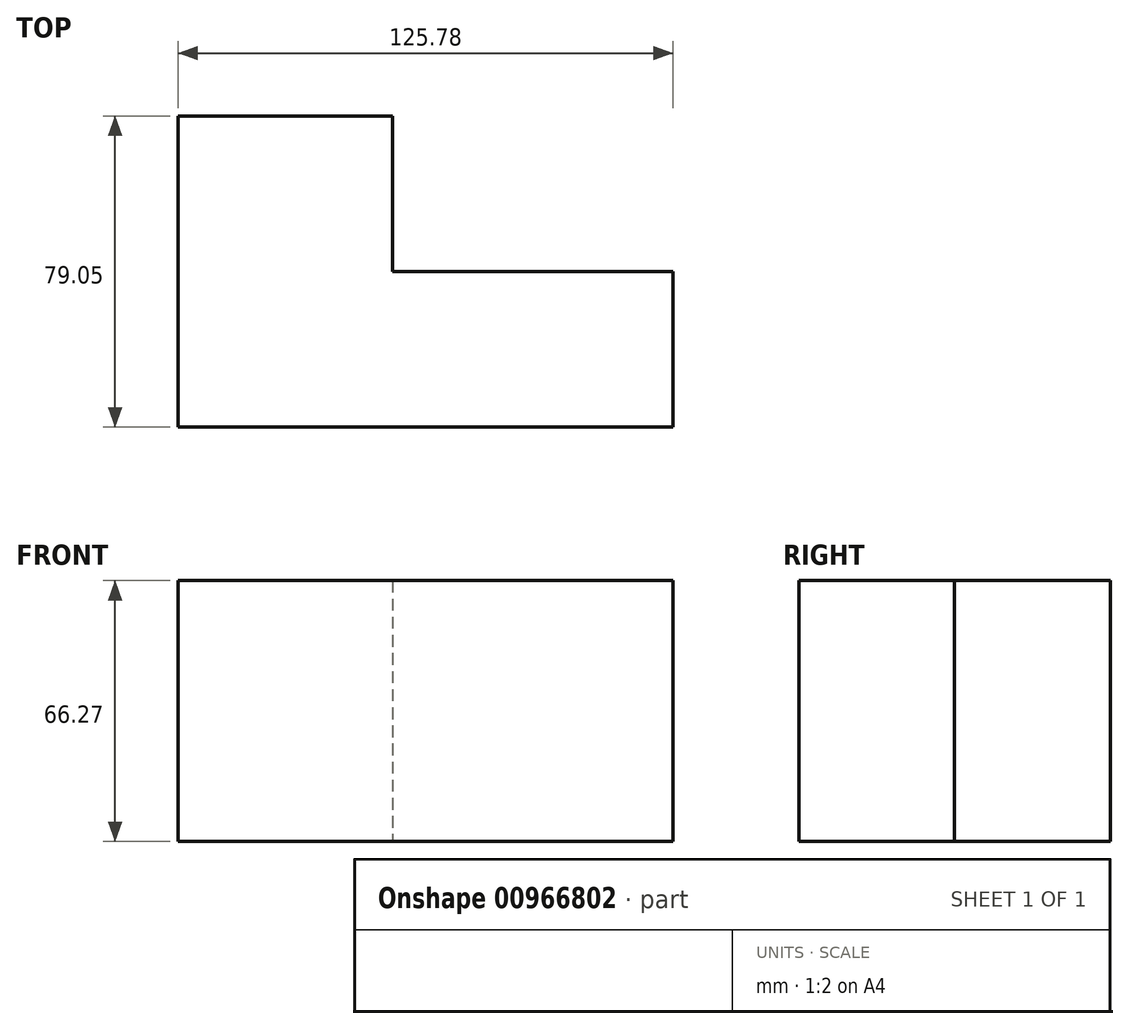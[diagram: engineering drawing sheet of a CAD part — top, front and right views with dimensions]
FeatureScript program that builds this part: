
annotation { "Feature Type Name" : "Feature", "Feature Type Description" : "" }
export const myFeature = defineFeature(function(context is Context, id is Id, definition is map)
    precondition{}
    {
        {
            var Q0;
            Q0=qCreatedBy(makeId("Top.planeOp"),FACE);
            var sketch = newSketch(context, id + "F0", { "sketchPlane" : qUnion([Q0])});
            skLineSegment(sketch, "E0.bottom", {"start": v(-8.37, 17.12) * mm, "end": v(197.72, 17.12) * mm});
            skLineSegment(sketch, "E0.top", {"start": v(-8.37, 162.04) * mm, "end": v(197.72, 162.04) * mm});
            skLineSegment(sketch, "E0.left", {"start": v(-8.37, 17.12) * mm, "end": v(-8.37, 162.04) * mm});
            skLineSegment(sketch, "E0.right", {"start": v(197.72, 17.12) * mm, "end": v(197.72, 162.04) * mm});
            skPoint(sketch, "E0.middle", {"position": v(94.68, 89.58) * mm});
            skLineSegment(sketch, "E1.bottom", {"start": v(62.89, 56.64) * mm, "end": v(-62.89, 56.64) * mm});
            skLineSegment(sketch, "E1.top", {"start": v(62.89, -22.4) * mm, "end": v(-62.89, -22.4) * mm});
            skLineSegment(sketch, "E1.left", {"start": v(62.89, 56.64) * mm, "end": v(62.89, -22.4) * mm});
            skLineSegment(sketch, "E1.right", {"start": v(-62.89, 56.64) * mm, "end": v(-62.89, -22.4) * mm});
            skPoint(sketch, "E1.middle", {"position": v(0, 17.12) * mm});
            skSolve(sketch);
        }
        {
            var Q0;
            {var subQ4=sQuery(id+"F0.wireOp",EDGE,"E1.top");Q0=makeQuery(id+"F0.imprint","IMPRINT",FACE,{"disambiguationData":[TD([[makeQuery(id+"F0.imprint","IMPRINT",EDGE,{"derivedFrom":subQ4}),-1.0]])]});}
            extrude(context, id + "F1", {"entities" : qUnion([Q0]), "depth" : 66.27 * mm, "offsetDistance" : 25.4 * mm});
        }
    });
